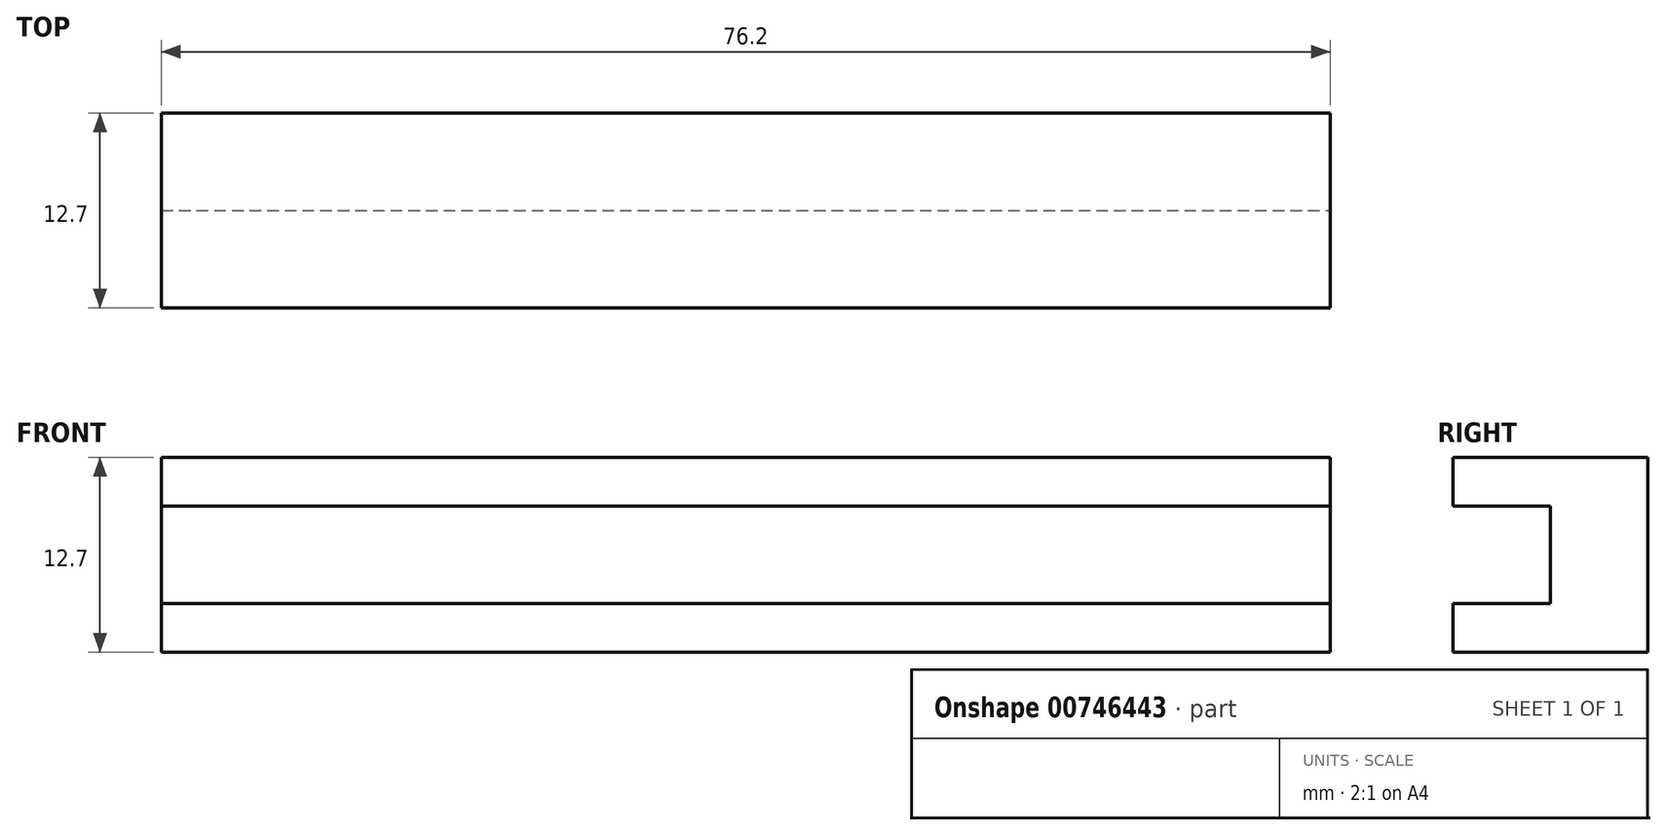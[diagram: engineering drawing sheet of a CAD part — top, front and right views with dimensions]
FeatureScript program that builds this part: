
annotation { "Feature Type Name" : "Feature", "Feature Type Description" : "" }
export const myFeature = defineFeature(function(context is Context, id is Id, definition is map)
    precondition{}
    {
        {
            var Q0;
            Q0=qCreatedBy(makeId("Front.planeOp"),FACE);
            var sketch = newSketch(context, id + "F0", { "sketchPlane" : qUnion([Q0])});
            skLineSegment(sketch, "E0.bottom", {"start": v(0, 0) * mm, "end": v(76.2, 0) * mm});
            skLineSegment(sketch, "E0.top", {"start": v(0, 12.7) * mm, "end": v(76.2, 12.7) * mm});
            skLineSegment(sketch, "E0.left", {"start": v(0, 0) * mm, "end": v(0, 12.7) * mm});
            skLineSegment(sketch, "E0.right", {"start": v(76.2, 0) * mm, "end": v(76.2, 12.7) * mm});
            skSolve(sketch);
        }
        {
            var Q0;
            Q0=makeQuery(id+"F0.imprint","IMPRINT",FACE,{"disambiguationData":[TD([[makeQuery(id+"F0.imprint","IMPRINT",EDGE,{"derivedFrom":sQuery(id+"F0.wireOp",EDGE,"E0.bottom")}),1.0]])]});
            extrude(context, id + "F1", {"entities" : qUnion([Q0]), "depth" : 6.35 * mm, "offsetDistance" : 25.4 * mm});
        }
        {
            var Q0;
            Q0=makeQuery(id+"F1.opExtrude","CAP_FACE",FACE,{"disambiguationData":[OSD([sQuery(id+"F0.wireOp",EDGE,"E0.bottom"),sQuery(id+"F0.wireOp",EDGE,"E0.top"),sQuery(id+"F0.wireOp",EDGE,"E0.left"),sQuery(id+"F0.wireOp",EDGE,"E0.right")])],"isStart":false});
            var sketch = newSketch(context, id + "F2", { "sketchPlane" : qUnion([Q0])});
            skLineSegment(sketch, "E1.0.0", {"start": v(76.2, 12.7) * mm, "end": v(0, 12.7) * mm});
            skLineSegment(sketch, "E1.0.1", {"start": v(0, 12.7) * mm, "end": v(0, 0) * mm});
            skLineSegment(sketch, "E1.0.2", {"start": v(0, 0) * mm, "end": v(76.2, 0) * mm});
            skLineSegment(sketch, "E1.0.3", {"start": v(76.2, 0) * mm, "end": v(76.2, 12.7) * mm});
            skLineSegment(sketch, "E2.0", {"start": v(76.2, 9.53) * mm, "end": v(0, 9.53) * mm});
            skLineSegment(sketch, "E3.0", {"start": v(0, 3.18) * mm, "end": v(76.2, 3.18) * mm});
            skSolve(sketch);
        }
        {
            var Q0;
            {var subQ0=sQuery(id+"F2.wireOp",EDGE,"E1.0.0");Q0=makeQuery(id+"F2.imprint","IMPRINT",FACE,{"disambiguationData":[TD([[makeQuery(id+"F2.imprint","IMPRINT",EDGE,{"derivedFrom":subQ0}),-1.0]])]});}
            var Q1;
            {var subQ0=sQuery(id+"F2.wireOp",EDGE,"E1.0.2");Q1=makeQuery(id+"F2.imprint","IMPRINT",FACE,{"disambiguationData":[TD([[makeQuery(id+"F2.imprint","IMPRINT",EDGE,{"derivedFrom":subQ0}),1.0]])]});}
            extrude(context, id + "F3", {"entities" : qUnion([Q0, Q1]), "operationType" : NewBodyOperationType.ADD, "depth" : 6.35 * mm, "offsetDistance" : 25.4 * mm});
        }
    });
